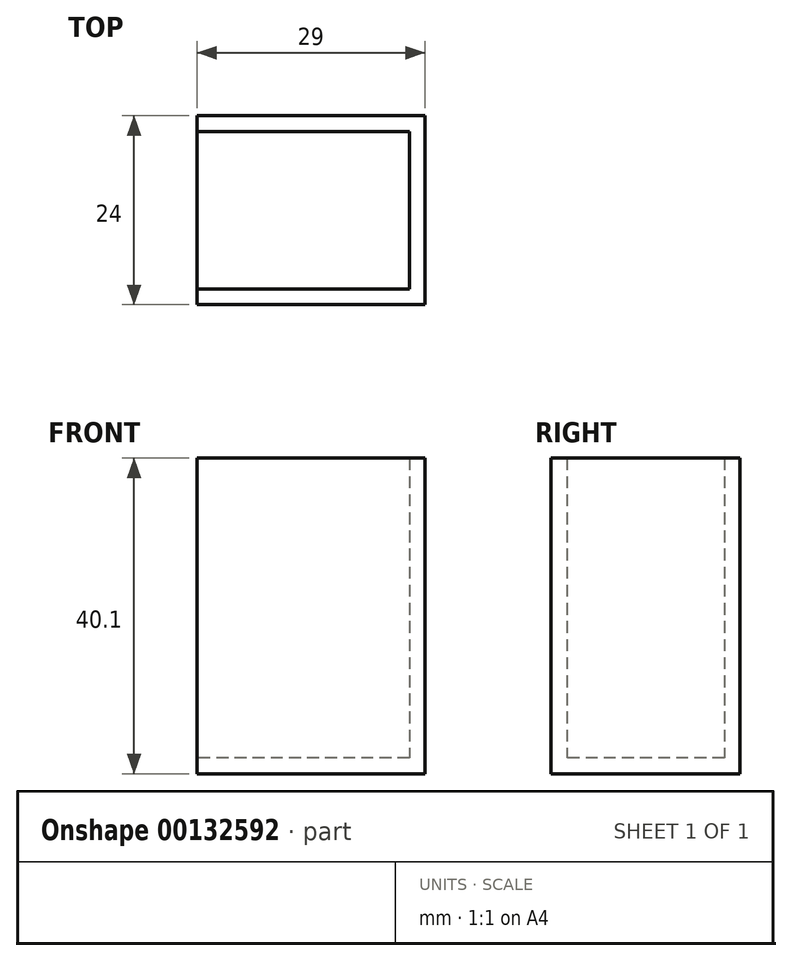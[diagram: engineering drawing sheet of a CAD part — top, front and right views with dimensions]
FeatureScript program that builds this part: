
annotation { "Feature Type Name" : "Feature", "Feature Type Description" : "" }
export const myFeature = defineFeature(function(context is Context, id is Id, definition is map)
    precondition{}
    {
        {
            var Q0;
            Q0=qCreatedBy(makeId("Top.planeOp"),FACE);
            var sketch = newSketch(context, id + "F0", { "sketchPlane" : qUnion([Q0])});
            skLineSegment(sketch, "E0.bottom", {"start": v(14.5, 12) * mm, "end": v(-14.5, 12) * mm});
            skLineSegment(sketch, "E0.top", {"start": v(14.5, -12) * mm, "end": v(-14.5, -12) * mm});
            skLineSegment(sketch, "E0.left", {"start": v(14.5, 12) * mm, "end": v(14.5, -12) * mm});
            skLineSegment(sketch, "E0.right", {"start": v(-14.5, 12) * mm, "end": v(-14.5, -12) * mm});
            skPoint(sketch, "E0.middle", {"position": v(0, 0) * mm});
            skLineSegment(sketch, "E1.bottom", {"start": v(12.5, 10) * mm, "end": v(-12.5, 10) * mm});
            skLineSegment(sketch, "E1.top", {"start": v(12.5, -10) * mm, "end": v(-12.5, -10) * mm});
            skLineSegment(sketch, "E1.left", {"start": v(12.5, 10) * mm, "end": v(12.5, -10) * mm});
            skLineSegment(sketch, "E1.right", {"start": v(-12.5, 10) * mm, "end": v(-12.5, -10) * mm});
            skSolve(sketch);
        }
        {
            var Q0;
            Q0=makeQuery(id+"F0.imprint","IMPRINT",FACE,{"disambiguationData":[TD([[makeQuery(id+"F0.imprint","IMPRINT",EDGE,{"derivedFrom":sQuery(id+"F0.wireOp",EDGE,"E0.bottom")}),1.0]])]});
            extrude(context, id + "F1", {"entities" : qUnion([Q0]), "depth" : 38.1 * mm});
        }
        {
            var Q0;
            Q0=makeQuery(id+"F0.imprint","IMPRINT",FACE,{"disambiguationData":[TD([[makeQuery(id+"F0.imprint","IMPRINT",EDGE,{"derivedFrom":sQuery(id+"F0.wireOp",EDGE,"E1.bottom")}),1.0]])]});
            var Q1;
            Q1=makeQuery(id+"F0.imprint","IMPRINT",FACE,{"disambiguationData":[TD([[makeQuery(id+"F0.imprint","IMPRINT",EDGE,{"derivedFrom":sQuery(id+"F0.wireOp",EDGE,"E0.bottom")}),1.0]])]});
            extrude(context, id + "F2", {"entities" : qUnion([Q0, Q1]), "operationType" : NewBodyOperationType.ADD, "oppositeDirection" : true, "depth" : 2 * mm});
        }
        {
            var Q0;
            {var subQ0=sQuery(id+"F0.wireOp",EDGE,"E0.right");Q0=makeQuery(id+"F2.boolean.opBoolean","MERGE",FACE,{"derivedFrom":[makeQuery(id+"F1.opExtrude","SWEPT_FACE",FACE,{"disambiguationData":[OSD([subQ0])]}),makeQuery(id+"F2.opExtrude","SWEPT_FACE",FACE,{"disambiguationData":[OSD([subQ0])]})]});}
            var sketch = newSketch(context, id + "F3", { "sketchPlane" : qUnion([Q0])});
            skLineSegment(sketch, "E2.bottom", {"start": v(-10, 38.1) * mm, "end": v(10, 38.1) * mm});
            skLineSegment(sketch, "E2.top", {"start": v(-10, 0) * mm, "end": v(10, 0) * mm});
            skLineSegment(sketch, "E2.left", {"start": v(-10, 38.1) * mm, "end": v(-10, 0) * mm});
            skLineSegment(sketch, "E2.right", {"start": v(10, 38.1) * mm, "end": v(10, 0) * mm});
            skSolve(sketch);
        }
        {
            var Q0;
            Q0=makeQuery(id+"F3.imprint","IMPRINT",FACE,{"disambiguationData":[TD([[makeQuery(id+"F3.imprint","IMPRINT",EDGE,{"derivedFrom":sQuery(id+"F3.wireOp",EDGE,"E2.bottom")}),-1.0]])]});
            extrude(context, id + "F4", {"entities" : qUnion([Q0]), "operationType" : NewBodyOperationType.REMOVE, "oppositeDirection" : true, "depth" : 2 * mm});
        }
    });
